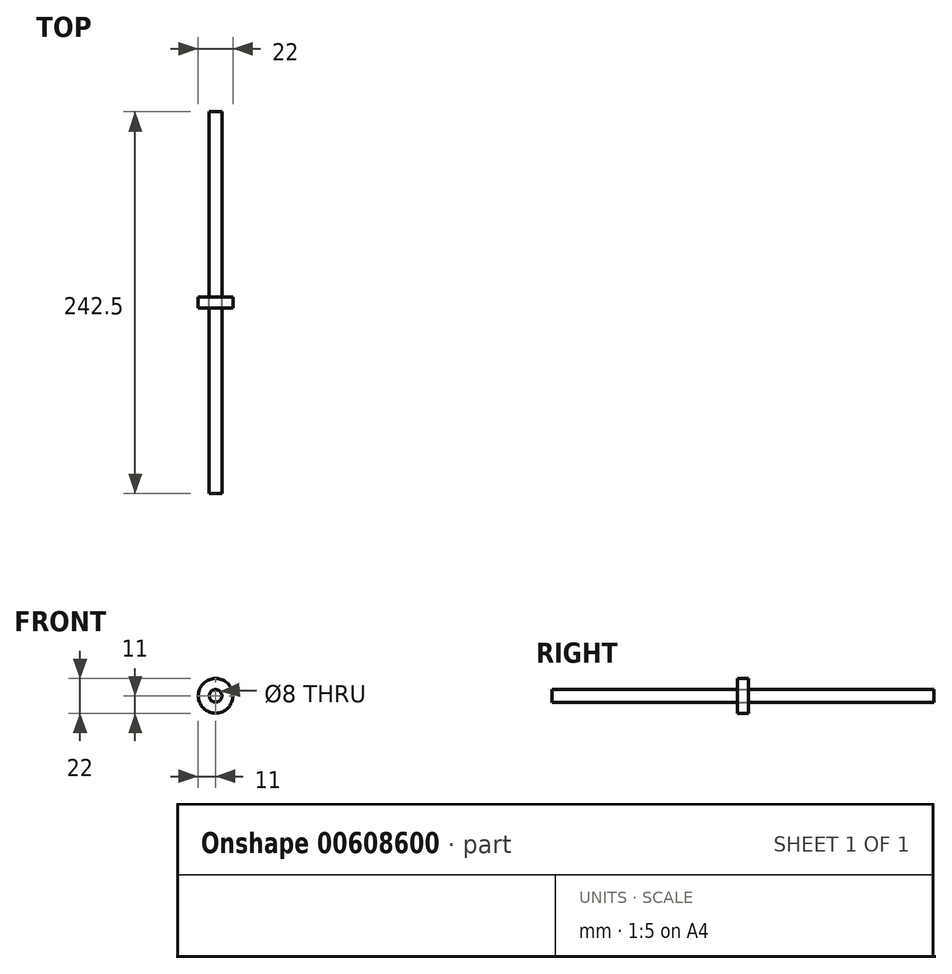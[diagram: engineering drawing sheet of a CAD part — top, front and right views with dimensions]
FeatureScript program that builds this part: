
annotation { "Feature Type Name" : "Feature", "Feature Type Description" : "" }
export const myFeature = defineFeature(function(context is Context, id is Id, definition is map)
    precondition{}
    {
        {
            var Q0;
            Q0=qCreatedBy(makeId("Front.planeOp"),FACE);
            var sketch = newSketch(context, id + "F0", { "sketchPlane" : qUnion([Q0])});
            skCircle(sketch, "E0", {"center": v(0, 0) * mm, "radius": 11 * mm});
            skCircle(sketch, "E1", {"center": v(0, 0) * mm, "radius": 4 * mm});
            skSolve(sketch);
        }
        {
            var Q0;
            Q0 = qSketchRegion(id + "F0", true);
            extrude(context, id + "F1", {"entities" : qUnion([Q0]), "endBound" : BoundingType.SYMMETRIC, "depth" : 7 * mm, "offsetDistance" : 25 * mm});
        }
        {
            var Q0;
            Q0=makeQuery(id+"F0.imprint","IMPRINT",FACE,{"disambiguationData":[TD([[makeQuery(id+"F0.imprint","IMPRINT",EDGE,{"derivedFrom":sQuery(id+"F0.wireOp",EDGE,"E1")}),1.0]])]});
            extrude(context, id + "F2", {"entities" : qUnion([Q0]), "endBound" : BoundingType.SYMMETRIC, "depth" : 242.5 * mm, "offsetDistance" : 25 * mm});
        }
    });
